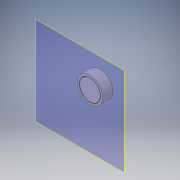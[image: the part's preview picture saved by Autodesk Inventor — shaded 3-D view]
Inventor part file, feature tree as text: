
AUTODESK INVENTOR PART (.ipt)
format: ipt  version: 2018 (Build 220112000, 112)  size: 109,568 bytes
history: native  units: in
note: dims shown in document units (in); Inventor stores cm internally (conversion verified against a paired STEP export)
features: extrude x2, sketch x2, plane x1
ambient origin geometry x8: Origin, YZ Plane, XZ Plane, XY Plane, X Axis, Y Axis, Z Axis, Center Point
bodies: Solid1 (feature_tree)
feature tree (5):
  extrude  "Extrusion1"  Depth=0.1in TaperAngle=0.0deg
  plane  "Work Plane1"
  extrude  "Extrusion4"  Depth=0.1in
  sketch  "Sketch1"  dims[d0=0.2in d1=0.1in d2=0.0in]
  sketch  "Sketch4"  dims[d13=0.21in d14=0.25in d15=0.1in d16=0.0in]
